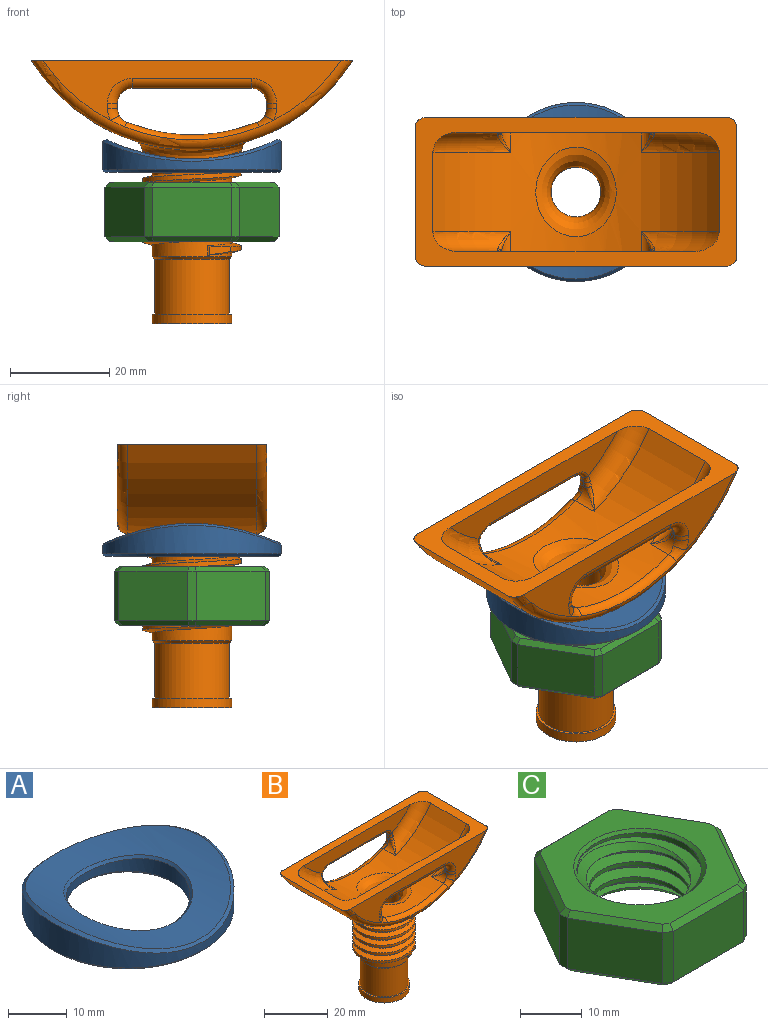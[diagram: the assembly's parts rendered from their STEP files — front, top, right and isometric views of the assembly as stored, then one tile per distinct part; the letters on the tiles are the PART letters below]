
ASSEMBLY  parts=3 mates=2
PART A: 8 faces, bbox 36x36x6.6 mm
  f0: cylinder r=40mm len=35.01mm, axis (0,1,0), area 595.8mm2, adj f6,f7
  f1: cylinder r=18mm len=36mm, axis (0,0,1), area 419.5mm2, adj f4,f7
  f2: plane 35x35mm, normal (0,0,-1), area 582mm2, adj f4,f5
  f3: cylinder r=10.5mm len=21mm, axis (0,0,1), area 214mm2, adj f5,f6
  f4: cone r=18mm half-angle=45deg, axis (0,0,1), area 78.9mm2, adj f1,f2
  f5: cone r=11mm half-angle=45deg, axis (0,0,-1), area 47.8mm2, adj f2,f3
  f6: bspline ~21.99x21.71mm, area 44.4mm2, adj f0,f3
  f7: bspline ~36.01x36mm, area 87.9mm2, adj f0,f1
PART B: 85 faces, bbox 70.6x31.1x57.5 mm
  f0: cylinder r=8mm len=16mm, axis (0,0,1), area 102.3mm2, adj f5,f6,f8,f19,f78
  f1: cylinder r=8mm len=16mm, axis (0,0,1), area 39.8mm2, adj f2,f6,f8,f81
  f2: cylinder r=8mm len=16mm, axis (0,0,1), area 55.3mm2, adj f1,f3,f6,f8
  f3: cylinder r=8mm len=16mm, axis (0,0,1), area 55.3mm2, adj f2,f4,f6,f8
  f4: cylinder r=8mm len=16mm, axis (0,0,1), area 55.5mm2, adj f3,f5,f6,f8
  f5: cylinder r=8mm len=16mm, axis (0,0,1), area 55mm2, adj f0,f4,f6,f8
  f6: bspline ~22.52x21.48mm, area 575.5mm2, adj f0,f1,f2,f3,f4,f5,f7,f78
  f7: cylinder r=9.9mm len=19.8mm, axis (0,0,1), area 313.7mm2, adj f6,f8,f79,f82
  f8: bspline ~22.52x21.48mm, area 626.8mm2, adj f0,f1,f2,f3,f4,f5,f7,f78
  f9: cylinder r=38mm len=64.71mm, axis (0,1,0), area 1578.5mm2, adj f11,f38,f39,f83
  f10: cylinder r=35mm len=57.54mm, axis (0,1,0), area 1133.7mm2, adj f11,f26,f27,f31,f32,f34,f35,f36
  f11: plane 65.24x30.53mm, normal (0,0,1), area 573.1mm2, adj f9,f10,f12,f13,f22,f25,f34,f35
  f12: plane 59.96x12.12mm, normal (0,-1,0), area 315.6mm2, adj f11,f39,f53,f54,f55,f56,f57,f58
  f13: plane 59.96x12.12mm, normal (0,1,0), area 315.6mm2, adj f11,f38,f43,f44,f45,f46,f47,f48
  f14: plane 16x16mm, normal (0,0,-1), area 122.5mm2, adj f15,f18
  f15: cylinder r=8mm len=16mm, axis (0,0,1), area 100.5mm2, adj f14,f16
  f16: plane 16x16mm, normal (0,0,1), area 24.3mm2, adj f15,f17
  f17: cylinder r=7.5mm len=15mm, axis (0,0,1), area 518.4mm2, adj f16,f19
  f18: cylinder r=5mm len=35.05mm, axis (0,0,1), area 1084.6mm2, adj f14,f84
  f19: cone r=8.5mm half-angle=45deg, axis (0,0,1), area 34.4mm2, adj f0,f17
  f20: plane 1.04x0.8mm, normal (1,0,0), area 0.6mm2, adj f30,f31,f46,f61
  f21: plane 1.04x0.8mm, normal (-1,0,0), area 0.6mm2, adj f32,f33,f45,f67
  f22: plane 47.49x6.88mm, normal (0,-1,0), area 213.3mm2, adj f11,f36,f37,f63,f64,f65
  f23: plane 1.04x0.8mm, normal (1,0,0), area 0.6mm2, adj f26,f29,f56,f70
  f24: plane 1.04x0.8mm, normal (-1,0,0), area 0.6mm2, adj f27,f28,f55,f76
  f25: plane 47.49x6.88mm, normal (0,1,0), area 213.3mm2, adj f11,f34,f35,f72,f73,f74
  f26: cylinder r=3mm len=5.27mm, axis (0,1,0), area 10.6mm2, adj f10,f23,f52,f54,f69
  f27: cylinder r=3mm len=5.27mm, axis (0,1,0), area 10.6mm2, adj f10,f24,f51,f53,f77
  f28: cylinder r=3mm len=1.36mm, axis (0,1,0), area 0.2mm2, adj f24,f57,f75
  f29: cylinder r=3mm len=1.36mm, axis (0,1,0), area 0.2mm2, adj f23,f58,f71
  f30: cylinder r=3mm len=1.36mm, axis (0,-1,0), area 0.2mm2, adj f20,f48,f62
  f31: cylinder r=3mm len=5.27mm, axis (0,1,0), area 10.6mm2, adj f10,f20,f42,f44,f60
  f32: cylinder r=3mm len=5.27mm, axis (0,1,0), area 10.6mm2, adj f10,f21,f41,f43,f68
  f33: cylinder r=3mm len=1.36mm, axis (0,-1,0), area 0.2mm2, adj f21,f47,f66
  f34: torus R=31mm, axis (0,-1,0), area 99mm2, adj f10,f11,f25,f69,f70,f71
  f35: torus R=31mm, axis (0,-1,0), area 99mm2, adj f10,f11,f25,f75,f76,f77
  f36: torus R=31mm, axis (0,1,0), area 99mm2, adj f10,f11,f22,f66,f67,f68
  f37: torus R=31mm, axis (0,1,0), area 99mm2, adj f10,f11,f22,f60,f61,f62
  f38: torus R=36mm, axis (0,-1,0), area 234.5mm2, adj f9,f11,f13,f40,f41,f42
  f39: torus R=36mm, axis (0,-1,0), area 234.5mm2, adj f9,f11,f12,f50,f51,f52
  f40: torus R=37mm, axis (0,1,0), area 56.9mm2, adj f10,f38,f41,f42
  f41: bspline ~3.78x2.6mm, area 5.9mm2, adj f32,f38,f40,f43
  f42: bspline ~3.78x2.6mm, area 5.9mm2, adj f31,f38,f40,f44
  f43: torus R=5mm, axis (0,-1,0), area 5.8mm2, adj f13,f32,f41,f45
  f44: torus R=5mm, axis (0,-1,0), area 5.8mm2, adj f13,f31,f42,f46
  f45: cylinder r=2mm len=2mm, axis (0,0,-1), area 3.3mm2, adj f13,f21,f43,f47
  f46: cylinder r=2mm len=2mm, axis (0,0,1), area 3.3mm2, adj f13,f20,f44,f48
  f47: torus R=5mm, axis (0,-1,0), area 18.4mm2, adj f13,f33,f45,f49,f65
  f48: torus R=5mm, axis (0,-1,0), area 18.4mm2, adj f13,f30,f46,f49,f63
  f49: cylinder r=2mm len=24mm, axis (1,0,0), area 75.4mm2, adj f13,f47,f48,f64
  f50: torus R=37mm, axis (0,-1,0), area 56.9mm2, adj f10,f39,f51,f52
  f51: bspline ~3.78x2.6mm, area 5.9mm2, adj f27,f39,f50,f53
  f52: bspline ~3.78x2.6mm, area 5.9mm2, adj f26,f39,f50,f54
  f53: torus R=5mm, axis (0,-1,0), area 5.8mm2, adj f12,f27,f51,f55
  f54: torus R=5mm, axis (0,-1,0), area 5.8mm2, adj f12,f26,f52,f56
  f55: cylinder r=2mm len=2mm, axis (0,0,1), area 3.3mm2, adj f12,f24,f53,f57
  f56: cylinder r=2mm len=2mm, axis (0,0,-1), area 3.3mm2, adj f12,f23,f54,f58
  f57: torus R=5mm, axis (0,-1,0), area 18.4mm2, adj f12,f28,f55,f59,f74
  f58: torus R=5mm, axis (0,-1,0), area 18.4mm2, adj f12,f29,f56,f59,f72
  f59: cylinder r=2mm len=24mm, axis (-1,0,0), area 75.4mm2, adj f12,f57,f58,f73
  f60: bspline ~4.57x3.87mm, area 2.4mm2, adj f31,f37,f61
  f61: bspline ~3.02x2.07mm, area 1.4mm2, adj f20,f37,f60,f62
  f62: bspline ~3.03x1.56mm, area 2.1mm2, adj f30,f37,f61,f63
  f63: torus R=4mm, axis (0,1,0), area 5.8mm2, adj f22,f48,f62,f64
  f64: cylinder r=1mm len=24mm, axis (1,0,0), area 37.7mm2, adj f22,f49,f63,f65
  f65: torus R=4mm, axis (0,1,0), area 5.8mm2, adj f22,f47,f64,f66
  f66: bspline ~3.03x1.56mm, area 2.1mm2, adj f33,f36,f65,f67
  f67: bspline ~2.32x1.64mm, area 1.4mm2, adj f21,f36,f66,f68
  f68: bspline ~4.57x3.87mm, area 2.4mm2, adj f32,f36,f67
  f69: bspline ~4.57x3.87mm, area 2.4mm2, adj f26,f34,f70
  f70: bspline ~2.32x1.64mm, area 1.4mm2, adj f23,f34,f69,f71
  f71: bspline ~3.03x1.56mm, area 2.1mm2, adj f29,f34,f70,f72
  f72: torus R=4mm, axis (0,-1,0), area 5.8mm2, adj f25,f58,f71,f73
  f73: cylinder r=1mm len=24mm, axis (1,0,0), area 37.7mm2, adj f25,f59,f72,f74
  f74: torus R=4mm, axis (0,-1,0), area 5.8mm2, adj f25,f57,f73,f75
  f75: bspline ~3.03x1.56mm, area 2.1mm2, adj f28,f35,f74,f76
  f76: bspline ~3.02x2.07mm, area 1.4mm2, adj f24,f35,f75,f77
  f77: bspline ~4.57x3.87mm, area 2.4mm2, adj f27,f35,f76
  f78: plane 1.91x0.38mm, normal (-0.3,-0.95,0), area 0.7mm2, adj f0,f6,f8,f79
  f79: plane 4.18x1.77mm, normal (0.29,-0.96,0), area 6.2mm2, adj f6,f7,f8,f78
  f80: cylinder r=10mm len=20mm, axis (0,0,-1), area 120.3mm2, adj f82,f83
  f81: plane 18.08x12.02mm, normal (0,0,-1), area 24.3mm2, adj f1,f6,f8,f82
  f82: cone r=10mm half-angle=45deg, axis (0,0,1), area 55.9mm2, adj f6,f7,f8,f80,f81
  f83: bspline ~24.03x22.81mm, area 190.2mm2, adj f9,f80
  f84: bspline ~18.03x16.17mm, area 229.7mm2, adj f10,f18
PART C: 46 faces, bbox 35x31.2x12.7 mm
  f0: plane 33x29.18mm, normal (0,0,1), area 376.3mm2, adj f5,f22,f23,f24,f25,f26,f27,f28
  f1: cylinder r=8.2mm len=16.4mm, axis (0,0,-1), area 96.3mm2, adj f3,f5,f6,f7,f9
  f2: plane 33x29.18mm, normal (0,0,-1), area 376.3mm2, adj f4,f34,f35,f36,f37,f38,f39,f40
  f3: cone r=8.2mm half-angle=45deg, axis (0,0,-1), area 16.7mm2, adj f1,f4,f7,f9
  f4: cone r=8.2mm half-angle=45deg, axis (0,0,-1), area 101.6mm2, adj f2,f3,f7,f8,f9
  f5: cone r=10.7mm half-angle=45deg, axis (0,0,1), area 116.8mm2, adj f0,f1,f6,f7,f8,f9
  f6: cone r=10.7mm half-angle=45deg, axis (0,0,1), area 1.5mm2, adj f1,f5,f9
  f7: bspline ~23.56x20.4mm, area 361.3mm2, adj f1,f3,f4,f5,f8
  f8: cylinder r=10.2mm len=20.4mm, axis (0,0,1), area 285.8mm2, adj f4,f5,f7,f9
  f9: bspline ~23.56x20.4mm, area 360.8mm2, adj f1,f3,f4,f5,f6,f8
  f10: plane 16x10mm, normal (0,1,0), area 160mm2, adj f16,f17,f24,f35
  f11: plane 13.86x10mm, normal (0.87,0.5,0), area 160mm2, adj f17,f18,f28,f39
  f12: plane 13.86x10mm, normal (0.87,-0.5,0), area 160mm2, adj f18,f20,f32,f43
  f13: plane 16x10mm, normal (0,-1,0), area 160mm2, adj f20,f21,f31,f44
  f14: plane 13.86x10mm, normal (-0.87,-0.5,0), area 160mm2, adj f19,f21,f27,f40
  f15: plane 13.86x10mm, normal (-0.87,0.5,0), area 160mm2, adj f16,f19,f23,f36
  f16: plane 10x1.5mm, normal (-0.5,0.87,0), area 17.3mm2, adj f10,f15,f22,f34
  f17: plane 10x1.5mm, normal (0.5,0.87,0), area 17.3mm2, adj f10,f11,f26,f37
  f18: plane 10x1.73mm, normal (1,0,0), area 17.3mm2, adj f11,f12,f30,f41
  f19: plane 10x1.73mm, normal (-1,0,0), area 17.3mm2, adj f14,f15,f25,f38
  f20: plane 10x1.5mm, normal (0.5,-0.87,0), area 17.3mm2, adj f12,f13,f33,f45
  f21: plane 10x1.5mm, normal (-0.5,-0.87,0), area 17.3mm2, adj f13,f14,f29,f42
  f22: plane 1.77x1.6mm, normal (-0.35,0.61,0.71), area 2.1mm2, adj f0,f16,f23,f24
  f23: plane 14.12x8.73mm, normal (-0.61,0.35,0.71), area 22.2mm2, adj f0,f15,f22,f25
  f24: plane 16x1mm, normal (0,0.71,0.71), area 22.2mm2, adj f0,f10,f22,f26
  f25: plane 1.73x1mm, normal (-0.71,0,0.71), area 2.1mm2, adj f0,f19,f23,f27
  f26: plane 1.77x1.6mm, normal (0.35,0.61,0.71), area 2.1mm2, adj f0,f17,f24,f28
  f27: plane 14.12x8.73mm, normal (-0.61,-0.35,0.71), area 22.2mm2, adj f0,f14,f25,f29
  f28: plane 14.12x8.73mm, normal (0.61,0.35,0.71), area 22.2mm2, adj f0,f11,f26,f30
  f29: plane 1.77x1.6mm, normal (-0.35,-0.61,0.71), area 2.1mm2, adj f0,f21,f27,f31
  f30: plane 1.73x1mm, normal (0.71,0,0.71), area 2.1mm2, adj f0,f18,f28,f32
  f31: plane 16x1mm, normal (0,-0.71,0.71), area 22.2mm2, adj f0,f13,f29,f33
  f32: plane 14.12x8.73mm, normal (0.61,-0.35,0.71), area 22.2mm2, adj f0,f12,f30,f33
  f33: plane 1.77x1.6mm, normal (0.35,-0.61,0.71), area 2.1mm2, adj f0,f20,f31,f32
  f34: plane 1.77x1.6mm, normal (-0.35,0.61,-0.71), area 2.1mm2, adj f2,f16,f35,f36
  f35: plane 16x1mm, normal (0,0.71,-0.71), area 22.2mm2, adj f2,f10,f34,f37
  f36: plane 14.12x8.73mm, normal (-0.61,0.35,-0.71), area 22.2mm2, adj f2,f15,f34,f38
  f37: plane 1.77x1.6mm, normal (0.35,0.61,-0.71), area 2.1mm2, adj f2,f17,f35,f39
  f38: plane 1.73x1mm, normal (-0.71,0,-0.71), area 2.1mm2, adj f2,f19,f36,f40
  f39: plane 14.12x8.73mm, normal (0.61,0.35,-0.71), area 22.2mm2, adj f2,f11,f37,f41
  f40: plane 14.12x8.73mm, normal (-0.61,-0.35,-0.71), area 22.2mm2, adj f2,f14,f38,f42
  f41: plane 1.73x1mm, normal (0.71,0,-0.71), area 2.1mm2, adj f2,f18,f39,f43
  f42: plane 1.77x1.6mm, normal (-0.35,-0.61,-0.71), area 2.1mm2, adj f2,f21,f40,f44
  f43: plane 14.12x8.73mm, normal (0.61,-0.35,-0.71), area 22.2mm2, adj f2,f12,f41,f45
  f44: plane 16x1mm, normal (0,-0.71,-0.71), area 22.2mm2, adj f2,f13,f42,f45
  f45: plane 1.77x1.6mm, normal (0.35,-0.61,-0.71), area 2.1mm2, adj f2,f20,f43,f44
PLACE A t=(0,0,-4.5)mm
PLACE B at identity fixed
PLACE C t=(0,0,-18.5)mm
MATE fastened C.f1 <-> A.f1  axis (0,0,1) through (0,0,-6.5)mm
MATE fastened A.f1 <-> B.f0  axis (0,0,1) through (0,0,-4)mm
